# Revit family: HVAC_Ductwork_Airzone_Round-Diffuser_DFCI1
name_source: partatom
category: Air Terminals
revit_build: Autodesk Revit 2016 (Build: 20161004_0715(x64)
units: mm (PartAtom-declared; Revit-internal decimal feet)

## family parameters
Always vertical = Yes
Cut with Voids When Loaded = No
OmniClass Number = 23.75.70.21.27.11
OmniClass Title = Diffusers, Registers, and Grilles
Part Type = Normal
Room Calculation Point = Yes
Round Connector Dimension = Use Diameter
Shared = No
Work Plane-Based = No

## types (1)
- INVALID TYPE - Use Load Family and Type Catalog instead
    Accessories Material = Metal - AIRZONE - Aluminium - Brushed
    Ak = 1.4
    Compatible Accesories = Insulated flexible duct (TFTA) and non-insulated flexible duct (TFST)
    Description = Round diffuser
    Disclaimer = All information provided in this model is reviewed before being published. However, Airzone cannot guarantee this model is error-free, therefore users are strongly encouraged to check for technical documentation and updates
    Duct Diameter = 150 mm
    Effective Area = 140.00 cm²
    Finish = White (RAL 9010)
    Fixing = Security mechanical attachment. Mounting bracket
    Long Description = Round diffuser DFCI to supply air in 4 directions that enables the air supply. Easy to disassemble to facilitate its maintenance. Designed to be installed in ceiling.
    Main Material = Metal - AIRZONE - Extruded Aluminium - White (RAL 9010)
    Manufacturer = AIRZONE
    Max Flow = 1500 m³/h
    Min Flow = 150 m³/h
    Model = INVALID – Type not loaded via type catalog
    Neck Length = 45.400 mm
    Product Code = INVALID – Type not loaded via type catalog
    Product Comments = Refer to technical documentation for further details
    Product Documentation Download URL = http://doc.airzone.es
    Revit Model Version = 1.0
    Type Image = <None>
    Type Image Comments = Image available in product documentation download
    URL = www.airzone.es
    c1 = 0.001601
    c2 = -3.153
    c3 = -153.1
    c4 = -77.45
    c5 = 82.34
    c6 = -6.299
    c7 = 0.01485
    c8 = -0.8079

## geometry (parser evidence)
native form markers: Extrusion x1, Sweep x2
no freeform markers — native parametric forms only
